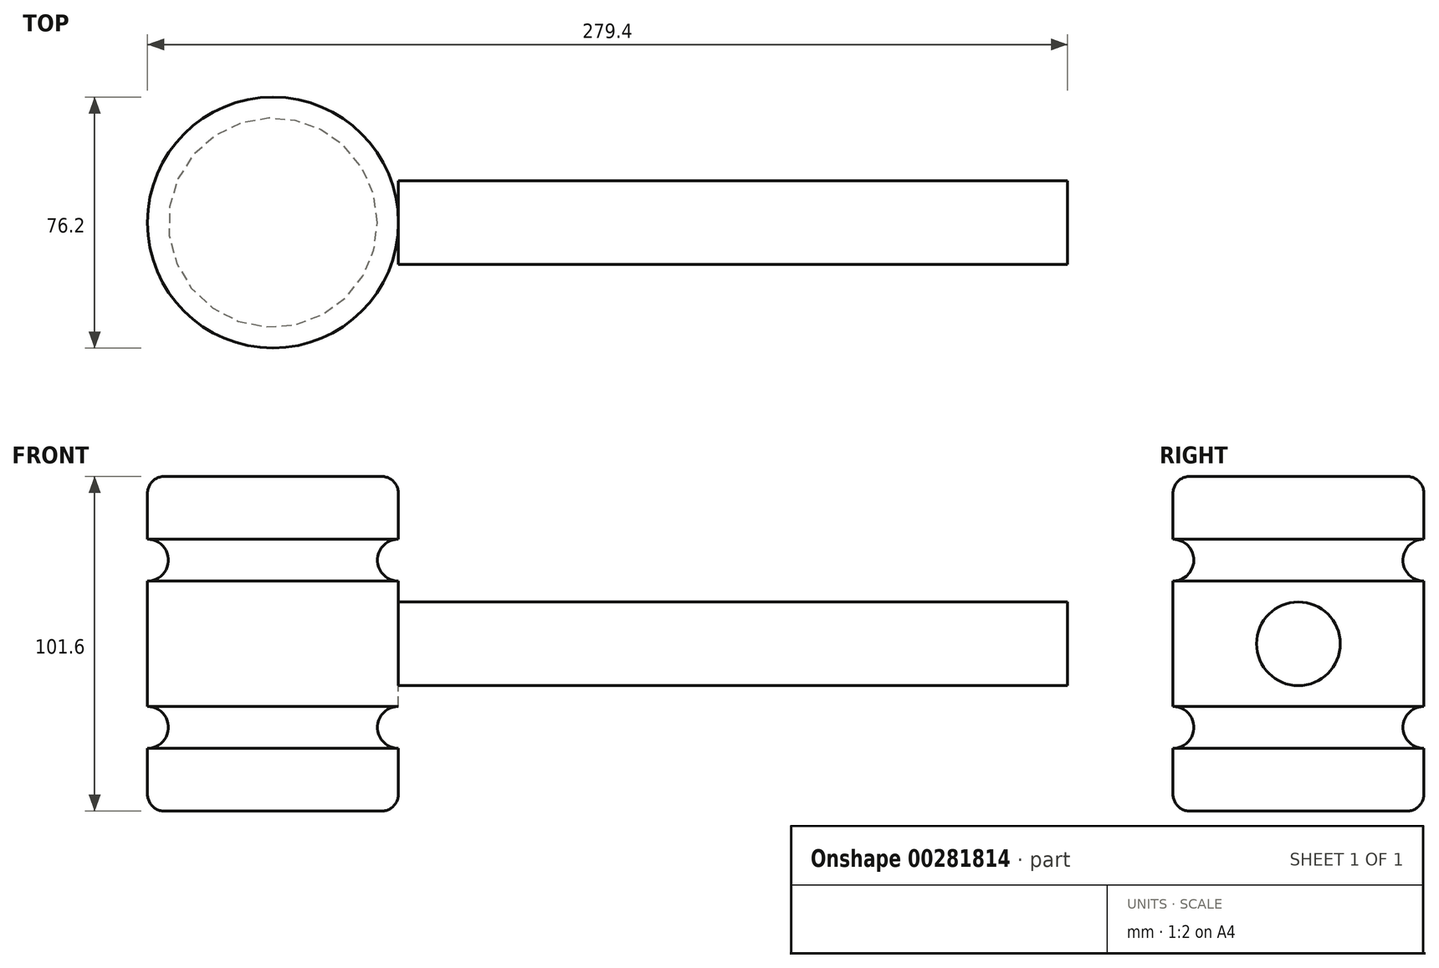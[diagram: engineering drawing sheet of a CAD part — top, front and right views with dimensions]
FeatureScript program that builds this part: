
annotation { "Feature Type Name" : "Feature", "Feature Type Description" : "" }
export const myFeature = defineFeature(function(context is Context, id is Id, definition is map)
    precondition{}
    {
        {
            var Q0;
            Q0=qCreatedBy(makeId("Front.planeOp"),FACE);
            var sketch = newSketch(context, id + "F0", { "sketchPlane" : qUnion([Q0])});
            skLineSegment(sketch, "E0", {"start": v(0, 0) * mm, "end": v(0, 19.05) * mm});
            skLineSegment(sketch, "E1", {"start": v(0, 101.6) * mm, "end": v(-38.1, 101.6) * mm});
            skLineSegment(sketch, "E2", {"start": v(-38.1, 101.6) * mm, "end": v(-38.1, 0) * mm});
            skLineSegment(sketch, "E3", {"start": v(-38.1, 0) * mm, "end": v(0, 0) * mm});
            skArc(sketch, "E4", {"start": v(0, 82.55) * mm, "mid": v(-6.35, 76.2) * mm, "end": v(0, 69.85) * mm});
            skArc(sketch, "E5", {"start": v(0, 31.75) * mm, "mid": v(-6.35, 25.4) * mm, "end": v(0, 19.05) * mm});
            skLineSegment(sketch, "E6.trimOffspring", {"start": v(0, 82.55) * mm, "end": v(0, 101.6) * mm});
            skLineSegment(sketch, "E7.trimOffspring", {"start": v(0, 31.75) * mm, "end": v(0, 69.85) * mm});
            skSolve(sketch);
        }
        {
            var Q0;
            Q0=makeQuery(id+"F0.imprint","IMPRINT",FACE,{"disambiguationData":[TD([[makeQuery(id+"F0.imprint","IMPRINT",EDGE,{"derivedFrom":sQuery(id+"F0.wireOp",EDGE,"E0")}),1.0]])]});
            var Q1;
            Q1=sQuery(id+"F0.wireOp",EDGE,"E2");
            revolve(context, id + "F1", {"entities" : qUnion([Q0]), "axis" : qUnion([Q1]), "revolveType" : RevolveType.FULL});
        }
        {
            var Q0;
            Q0=makeQuery(id+"F1.opRevolve","SWEPT_EDGE",EDGE,{"disambiguationData":[OSD([sQuery(id+"F0.wireOp",EDGE,"E1"),sQuery(id+"F0.wireOp",EDGE,"E6.trimOffspring")])]});
            var Q1;
            Q1=makeQuery(id+"F1.opRevolve","SWEPT_EDGE",EDGE,{"disambiguationData":[OSD([sQuery(id+"F0.wireOp",EDGE,"E0"),sQuery(id+"F0.wireOp",EDGE,"E3")])]});
            fillet(context, id + "F2", {"entities" : qUnion([Q0, Q1]), "radius" : 5.08 * mm, "tangentPropagation" : true, "allowEdgeOverflow" : false});
        }
        {
            var Q0;
            Q0=qCreatedBy(makeId("Right.planeOp"),FACE);
            var sketch = newSketch(context, id + "F3", { "sketchPlane" : qUnion([Q0])});
            skCircle(sketch, "E8", {"center": v(0, 50.8) * mm, "radius": 12.7 * mm});
            skSolve(sketch);
        }
        {
            var Q0;
            Q0 = qSketchRegion(id + "F3", true);
            extrude(context, id + "F4", {"entities" : qUnion([Q0]), "operationType" : NewBodyOperationType.ADD, "depth" : 203.2 * mm});
        }
    });
